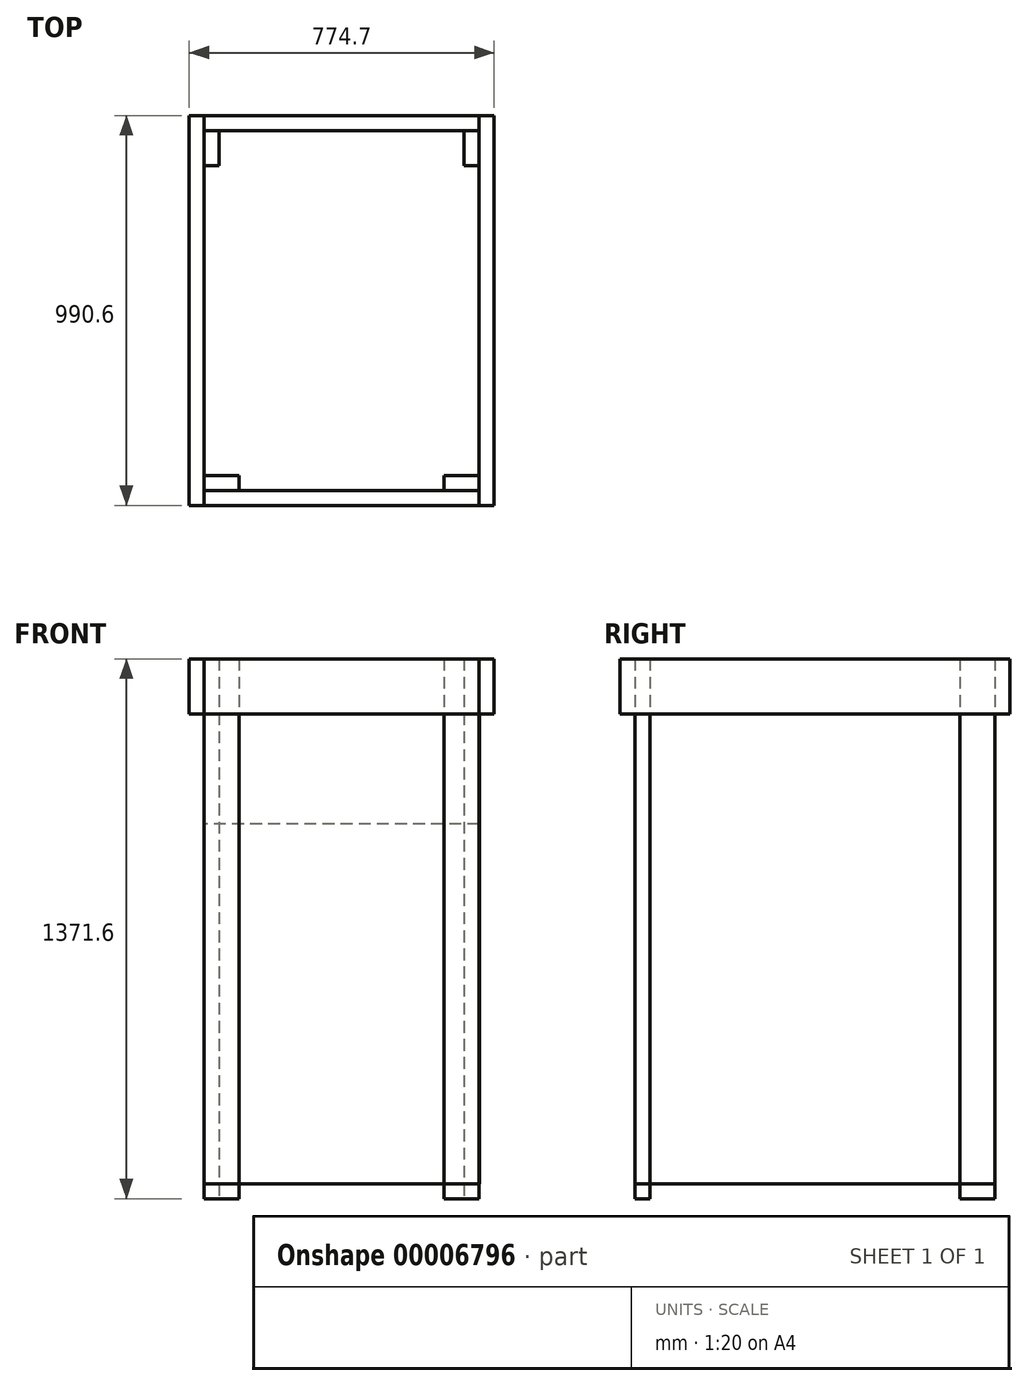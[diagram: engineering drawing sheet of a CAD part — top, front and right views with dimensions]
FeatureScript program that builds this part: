
annotation { "Feature Type Name" : "Feature", "Feature Type Description" : "" }
export const myFeature = defineFeature(function(context is Context, id is Id, definition is map)
    precondition{}
    {
        {
            var Q0;
            Q0=qCreatedBy(makeId("Top.planeOp"),FACE);
            var sketch = newSketch(context, id + "F0", { "sketchPlane" : qUnion([Q0])});
            skLineSegment(sketch, "E0.rect.bottom", {"start": v(349.25, 457.2) * mm, "end": v(-349.25, 457.2) * mm, "construction": true});
            skLineSegment(sketch, "E0.rect.top", {"start": v(349.25, -457.2) * mm, "end": v(-349.25, -457.2) * mm, "construction": true});
            skLineSegment(sketch, "E0.rect.left", {"start": v(349.25, 457.2) * mm, "end": v(349.25, -457.2) * mm, "construction": true});
            skLineSegment(sketch, "E0.rect.right", {"start": v(-349.25, 457.2) * mm, "end": v(-349.25, -457.2) * mm, "construction": true});
            skPoint(sketch, "E0.rect.middle", {"position": v(0, 0) * mm});
            skLineSegment(sketch, "E1.bottom", {"start": v(-349.25, 457.2) * mm, "end": v(-311.15, 457.2) * mm});
            skLineSegment(sketch, "E1.top", {"start": v(-349.25, 368.3) * mm, "end": v(-311.15, 368.3) * mm});
            skLineSegment(sketch, "E1.left", {"start": v(-349.25, 457.2) * mm, "end": v(-349.25, 368.3) * mm});
            skLineSegment(sketch, "E1.right", {"start": v(-311.15, 457.2) * mm, "end": v(-311.15, 368.3) * mm});
            skLineSegment(sketch, "E2", {"start": v(0, 457.2) * mm, "end": v(0, -457.2) * mm, "construction": true});
            skLineSegment(sketch, "E3.bottom", {"start": v(-349.25, -457.2) * mm, "end": v(-260.35, -457.2) * mm});
            skLineSegment(sketch, "E3.top", {"start": v(-349.25, -419.1) * mm, "end": v(-260.35, -419.1) * mm});
            skLineSegment(sketch, "E3.left", {"start": v(-349.25, -457.2) * mm, "end": v(-349.25, -419.1) * mm});
            skLineSegment(sketch, "E3.right", {"start": v(-260.35, -457.2) * mm, "end": v(-260.35, -419.1) * mm});
            skLineSegment(sketch, "E4.0.MirrorCS", {"start": v(311.15, 457.2) * mm, "end": v(311.15, 368.3) * mm});
            skLineSegment(sketch, "E5.0.MirrorCS", {"start": v(349.25, 457.2) * mm, "end": v(311.15, 457.2) * mm});
            skLineSegment(sketch, "E6.0.MirrorCS", {"start": v(349.25, 457.2) * mm, "end": v(349.25, 368.3) * mm});
            skLineSegment(sketch, "E7.0.MirrorCS", {"start": v(349.25, 368.3) * mm, "end": v(311.15, 368.3) * mm});
            skLineSegment(sketch, "E8.0.MirrorCS", {"start": v(260.35, -457.2) * mm, "end": v(260.35, -419.1) * mm});
            skLineSegment(sketch, "E9.0.MirrorCS", {"start": v(349.25, -457.2) * mm, "end": v(260.35, -457.2) * mm});
            skLineSegment(sketch, "E10.0.MirrorCS", {"start": v(349.25, -419.1) * mm, "end": v(260.35, -419.1) * mm});
            skLineSegment(sketch, "E11.0.MirrorCS", {"start": v(349.25, -457.2) * mm, "end": v(349.25, -419.1) * mm});
            skSolve(sketch);
        }
        {
            var Q0;
            Q0 = qSketchRegion(id + "F0", true);
            extrude(context, id + "F1", {"entities" : qUnion([Q0]), "depth" : 1371.6 * mm});
        }
        {
            var Q0;
            Q0=makeQuery(id+"F1.opExtrude","SWEPT_FACE",FACE,{"disambiguationData":[OSD([sQuery(id+"F0.wireOp",EDGE,"E1.left")])]});
            var sketch = newSketch(context, id + "F2", { "sketchPlane" : qUnion([Q0])});
            skLineSegment(sketch, "E12.bottom", {"start": v(-495.3, 1231.9) * mm, "end": v(495.3, 1231.9) * mm});
            skLineSegment(sketch, "E12.top", {"start": v(-495.3, 1371.6) * mm, "end": v(495.3, 1371.6) * mm});
            skLineSegment(sketch, "E12.left", {"start": v(-495.3, 1231.9) * mm, "end": v(-495.3, 1371.6) * mm});
            skLineSegment(sketch, "E12.right", {"start": v(495.3, 1231.9) * mm, "end": v(495.3, 1371.6) * mm});
            skSolve(sketch);
        }
        {
            var Q0;
            Q0 = qSketchRegion(id + "F2", true);
            extrude(context, id + "F3", {"entities" : qUnion([Q0]), "depth" : 38.1 * mm});
        }
        {
            var Q0;
            Q0=makeQuery(id+"F1.opExtrude","SWEPT_FACE",FACE,{"disambiguationData":[OSD([sQuery(id+"F0.wireOp",EDGE,"E3.bottom")])]});
            var sketch = newSketch(context, id + "F4", { "sketchPlane" : qUnion([Q0])});
            skLineSegment(sketch, "E13.bottom", {"start": v(-349.25, 1231.9) * mm, "end": v(349.25, 1231.9) * mm});
            skLineSegment(sketch, "E13.top", {"start": v(-349.25, 1371.6) * mm, "end": v(349.25, 1371.6) * mm});
            skLineSegment(sketch, "E13.left", {"start": v(-349.25, 1231.9) * mm, "end": v(-349.25, 1371.6) * mm});
            skLineSegment(sketch, "E13.right", {"start": v(349.25, 1231.9) * mm, "end": v(349.25, 1371.6) * mm});
            skSolve(sketch);
        }
        {
            var Q0;
            Q0 = qSketchRegion(id + "F4", true);
            extrude(context, id + "F5", {"entities" : qUnion([Q0]), "depth" : 38.1 * mm});
        }
        {
            var Q0;
            Q0=makeQuery(id+"F1.opExtrude","SWEPT_FACE",FACE,{"disambiguationData":[OSD([sQuery(id+"F0.wireOp",EDGE,"E1.left")])]});
            var sketch = newSketch(context, id + "F6", { "sketchPlane" : qUnion([Q0])});
            skLineSegment(sketch, "E14.bottom", {"start": v(-457.2, 1231.9) * mm, "end": v(457.2, 1231.9) * mm});
            skLineSegment(sketch, "E14.top", {"start": v(-457.2, 38.1) * mm, "end": v(457.2, 38.1) * mm});
            skLineSegment(sketch, "E14.left", {"start": v(-457.2, 1231.9) * mm, "end": v(-457.2, 38.1) * mm});
            skLineSegment(sketch, "E14.right", {"start": v(457.2, 1231.9) * mm, "end": v(457.2, 38.1) * mm});
            skSolve(sketch);
        }
        {
            var Q0;
            Q0 = qSketchRegion(id + "F6", true);
            extrude(context, id + "F7", {"entities" : qUnion([Q0]), "depth" : 3 / 203.2 * mm});
        }
        {
            var Q0;
            Q0=makeQuery(id+"F1.opExtrude","SWEPT_FACE",FACE,{"disambiguationData":[OSD([sQuery(id+"F0.wireOp",EDGE,"E3.bottom")])]});
            var sketch = newSketch(context, id + "F8", { "sketchPlane" : qUnion([Q0])});
            skLineSegment(sketch, "E15.bottom", {"start": v(-349.25, 1231.9) * mm, "end": v(349.25, 1231.9) * mm});
            skLineSegment(sketch, "E15.top", {"start": v(-349.25, 38.1) * mm, "end": v(349.25, 38.1) * mm});
            skLineSegment(sketch, "E15.left", {"start": v(-349.25, 1231.9) * mm, "end": v(-349.25, 38.1) * mm});
            skLineSegment(sketch, "E15.right", {"start": v(349.25, 1231.9) * mm, "end": v(349.25, 38.1) * mm});
            skSolve(sketch);
        }
        {
            var Q0;
            Q0 = qSketchRegion(id + "F8", true);
            extrude(context, id + "F9", {"entities" : qUnion([Q0]), "depth" : 3 / 203.2 * mm});
        }
        {
            var Q0;
            Q0=makeQuery(id+"F3.opExtrude","SWEPT_BODY",BODY,{"disambiguationData":[OSD([sQuery(id+"F2.wireOp",EDGE,"E12.bottom"),sQuery(id+"F2.wireOp",EDGE,"E12.top"),sQuery(id+"F2.wireOp",EDGE,"E12.left"),sQuery(id+"F2.wireOp",EDGE,"E12.right")])]});
            var Q1;
            Q1=makeQuery(id+"F7.opExtrude","SWEPT_BODY",BODY,{"disambiguationData":[OSD([sQuery(id+"F6.wireOp",EDGE,"E14.bottom"),sQuery(id+"F6.wireOp",EDGE,"E14.top"),sQuery(id+"F6.wireOp",EDGE,"E14.left"),sQuery(id+"F6.wireOp",EDGE,"E14.right")])]});
            var Q2;
            Q2=qCreatedBy(makeId("Right.planeOp"),FACE);
            mirror(context, id + "F10", {"entities" : qUnion([Q0, Q1]), "mirrorPlane" : qUnion([Q2])});
        }
        {
            var Q0;
            Q0=makeQuery(id+"F5.opExtrude","SWEPT_BODY",BODY,{"disambiguationData":[OSD([sQuery(id+"F4.wireOp",EDGE,"E13.bottom"),sQuery(id+"F4.wireOp",EDGE,"E13.top"),sQuery(id+"F4.wireOp",EDGE,"E13.left"),sQuery(id+"F4.wireOp",EDGE,"E13.right")])]});
            var Q1;
            Q1=makeQuery(id+"F9.opExtrude","SWEPT_BODY",BODY,{"disambiguationData":[OSD([sQuery(id+"F8.wireOp",EDGE,"E15.bottom"),sQuery(id+"F8.wireOp",EDGE,"E15.top"),sQuery(id+"F8.wireOp",EDGE,"E15.left"),sQuery(id+"F8.wireOp",EDGE,"E15.right")])]});
            var Q2;
            Q2=qCreatedBy(makeId("Front.planeOp"),FACE);
            mirror(context, id + "F11", {"entities" : qUnion([Q0, Q1]), "mirrorPlane" : qUnion([Q2])});
        }
        {
            var Q0;
            Q0=makeQuery(id+"F11.opPattern","COPY",FACE,{"derivedFrom":makeQuery(id+"F9.opExtrude","CAP_FACE",FACE,{"disambiguationData":[OSD([sQuery(id+"F8.wireOp",EDGE,"E15.bottom"),sQuery(id+"F8.wireOp",EDGE,"E15.top"),sQuery(id+"F8.wireOp",EDGE,"E15.left"),sQuery(id+"F8.wireOp",EDGE,"E15.right")])],"isStart":false}),"instanceName":"1"});
            var sketch = newSketch(context, id + "F12", { "sketchPlane" : qUnion([Q0])});
            skLineSegment(sketch, "E16.bottom", {"start": v(-349.25, 952.5) * mm, "end": v(349.25, 952.5) * mm});
            skLineSegment(sketch, "E16.top", {"start": v(-349.25, 38.1) * mm, "end": v(349.25, 38.1) * mm});
            skLineSegment(sketch, "E16.left", {"start": v(-349.25, 952.5) * mm, "end": v(-349.25, 38.1) * mm});
            skLineSegment(sketch, "E16.right", {"start": v(349.25, 952.5) * mm, "end": v(349.25, 38.1) * mm});
            skPoint(sketch, "E17", {"position": v(0, 38.1) * mm});
            skSolve(sketch);
        }
        {
            var Q0;
            Q0 = qSketchRegion(id + "F12", true);
            extrude(context, id + "F13", {"entities" : qUnion([Q0]), "operationType" : NewBodyOperationType.REMOVE, "endBound" : BoundingType.UP_TO_NEXT, "oppositeDirection" : true, "depth" : 25.4 * mm});
        }
    });
